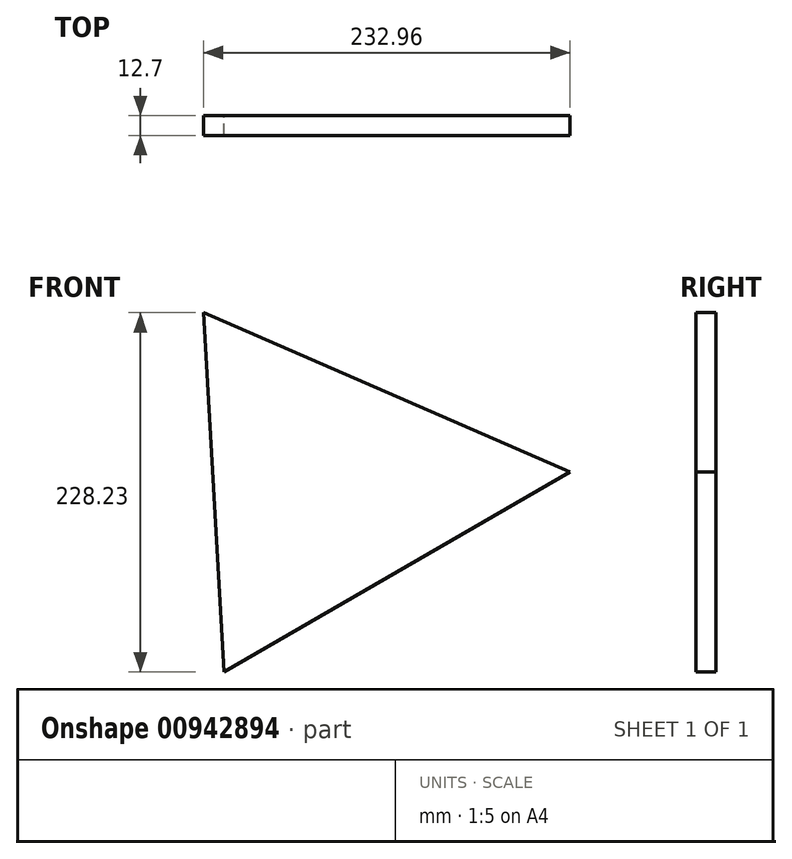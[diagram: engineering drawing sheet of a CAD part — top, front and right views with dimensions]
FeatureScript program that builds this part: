
annotation { "Feature Type Name" : "Feature", "Feature Type Description" : "" }
export const myFeature = defineFeature(function(context is Context, id is Id, definition is map)
    precondition{}
    {
        {
            var Q0;
            Q0=qCreatedBy(makeId("Front.planeOp"),FACE);
            var sketch = newSketch(context, id + "F0", { "sketchPlane" : qUnion([Q0])});
            skLineSegment(sketch, "E0", {"start": v(-144.97, 101.22) * mm, "end": v(-131.98, -127) * mm});
            skLineSegment(sketch, "E1", {"start": v(-131.98, -127) * mm, "end": v(88, 0) * mm});
            skLineSegment(sketch, "E2", {"start": v(88, 0) * mm, "end": v(-144.97, 101.22) * mm});
            skSolve(sketch);
        }
        {
            var Q0;
            Q0 = qSketchRegion(id + "F0", true);
            extrude(context, id + "F1", {"entities" : qUnion([Q0]), "depth" : 12.7 * mm, "offsetDistance" : 25.4 * mm});
        }
    });
